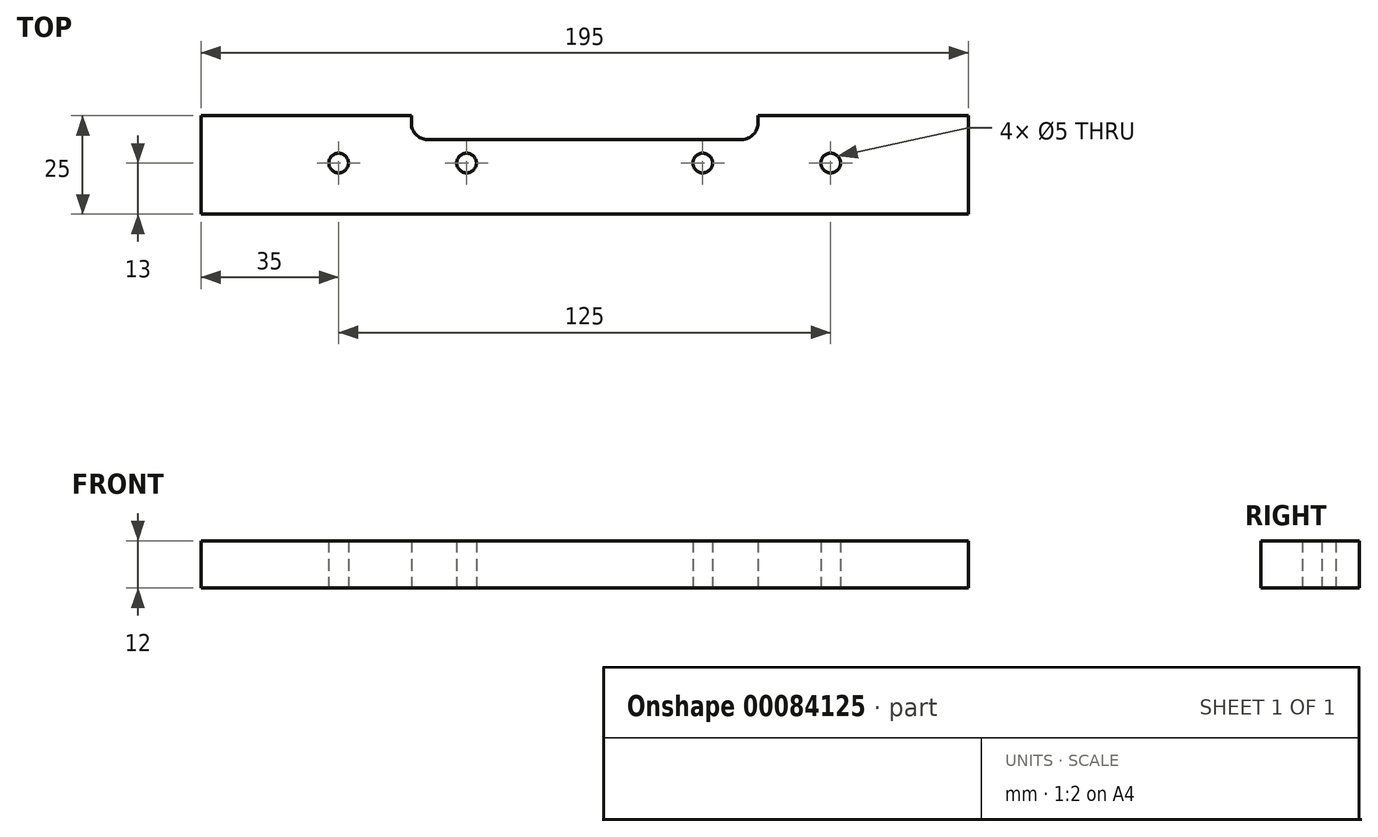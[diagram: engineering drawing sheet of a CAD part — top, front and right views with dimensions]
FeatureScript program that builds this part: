
annotation { "Feature Type Name" : "Feature", "Feature Type Description" : "" }
export const myFeature = defineFeature(function(context is Context, id is Id, definition is map)
    precondition{}
    {
        {
            var Q0;
            Q0=qCreatedBy(makeId("Top.planeOp"),FACE);
            var sketch = newSketch(context, id + "F0", { "sketchPlane" : qUnion([Q0])});
            skLineSegment(sketch, "E0.bottom", {"start": v(97.5, -12.5) * mm, "end": v(-97.5, -12.5) * mm});
            skLineSegment(sketch, "E0.top", {"start": v(97.5, 12.5) * mm, "end": v(-97.5, 12.5) * mm});
            skLineSegment(sketch, "E0.left", {"start": v(97.5, -12.5) * mm, "end": v(97.5, 12.5) * mm});
            skLineSegment(sketch, "E0.right", {"start": v(-97.5, -12.5) * mm, "end": v(-97.5, 12.5) * mm});
            skPoint(sketch, "E0.middle", {"position": v(0, 0) * mm});
            skLineSegment(sketch, "E1", {"start": v(-97.5, 0.5) * mm, "end": v(97.5, 0.5) * mm, "construction": true});
            skPoint(sketch, "E2", {"position": v(-30, 0.5) * mm});
            skPoint(sketch, "E3", {"position": v(-62.5, 0.5) * mm});
            skPoint(sketch, "E4", {"position": v(30, 0.5) * mm});
            skPoint(sketch, "E5", {"position": v(62.5, 0.5) * mm});
            skCircle(sketch, "E6", {"center": v(-62.5, 0.5) * mm, "radius": 2.5 * mm});
            skCircle(sketch, "E7", {"center": v(-30, 0.5) * mm, "radius": 2.5 * mm});
            skCircle(sketch, "E8", {"center": v(30, 0.5) * mm, "radius": 2.5 * mm});
            skCircle(sketch, "E9", {"center": v(62.5, 0.5) * mm, "radius": 2.5 * mm});
            skLineSegment(sketch, "E10.bottom", {"start": v(44, 6.5) * mm, "end": v(-44, 6.5) * mm});
            skLineSegment(sketch, "E10.top", {"start": v(44, 18.5) * mm, "end": v(-44, 18.5) * mm});
            skLineSegment(sketch, "E10.left", {"start": v(44, 6.5) * mm, "end": v(44, 18.5) * mm});
            skLineSegment(sketch, "E10.right", {"start": v(-44, 6.5) * mm, "end": v(-44, 18.5) * mm});
            skPoint(sketch, "E10.middle", {"position": v(0, 12.5) * mm});
            skSolve(sketch);
        }
        {
            var Q0;
            Q0=makeQuery(id+"F0.imprint","IMPRINT",FACE,{"disambiguationData":[TD([[makeQuery(id+"F0.imprint","IMPRINT",EDGE,{"derivedFrom":sQuery(id+"F0.wireOp",EDGE,"E0.bottom")}),-1.0]])]});
            extrude(context, id + "F1", {"entities" : qUnion([Q0]), "depth" : 12 * mm});
        }
        {
            var Q0;
            Q0=makeQuery(id+"F1.opExtrude","SWEPT_EDGE",EDGE,{"disambiguationData":[OSD([sQuery(id+"F0.wireOp",EDGE,"E10.bottom"),sQuery(id+"F0.wireOp",EDGE,"E10.right")])]});
            var Q1;
            Q1=makeQuery(id+"F1.opExtrude","SWEPT_EDGE",EDGE,{"disambiguationData":[OSD([sQuery(id+"F0.wireOp",EDGE,"E10.bottom"),sQuery(id+"F0.wireOp",EDGE,"E10.left")])]});
            fillet(context, id + "F2", {"entities" : qUnion([Q0, Q1]), "radius" : 4 * mm, "tangentPropagation" : true, "allowEdgeOverflow" : false});
        }
    });
